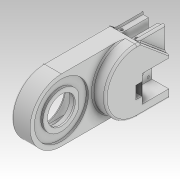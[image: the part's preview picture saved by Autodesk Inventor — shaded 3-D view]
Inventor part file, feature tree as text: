
AUTODESK INVENTOR PART (.ipt)
format: ipt  version: 2020 (Build 240168000, 168)  size: 802,304 bytes
history: native  units: mm
features: sketch x33, extrude x31, chamfer x4, fillet x3, plane x2, revolve x2, projected_geometry x1
ambient origin geometry x8: Origin, YZ Plane, XZ Plane, XY Plane, X Axis, Y Axis, Z Axis, Center Point
bodies: Solid1 (feature_tree)
feature tree (76):
  extrude  "Extrusion1"  Depth=50.0mm
  extrude  "Extrusion3"  Depth=50.0mm TaperAngle=0.0deg
  extrude  "Extrusion6"  TaperAngle=0.0deg  [1 undecoded]
  extrude  "Extrusion7"  Depth=50.0mm
  extrude  "Extrusion8"  Depth=10.0mm TaperAngle=0.0deg
  extrude  "Extrusion9"  TaperAngle=0.0deg  [1 undecoded]
  extrude  "Extrusion10"  TaperAngle=30.0deg  [1 undecoded]
  extrude  "Extrusion11"  Depth=16.15mm
  extrude  "Extrusion12"  Depth=60.0mm
  plane  "Work Plane1"
  extrude  "Extrusion13"  Depth=10.0mm TaperAngle=0.0deg
  revolve  "Revolution1"  [1 undecoded]
  extrude  "Extrusion14"  Depth=86.0mm
  extrude  "Extrusion15"  Depth=3.5mm TaperAngle=0.0deg
  extrude  "Extrusion16"  Depth=75.0mm
  revolve  "Revolution2"  [1 undecoded]
  extrude  "Extrusion17"  Depth=1.5mm
  fillet  "Fillet1"  [1 undecoded]
  plane  "Work Plane2"
  extrude  "Extrusion18"  Depth=31.0mm
  extrude  "Extrusion19"  Depth=3.0mm TaperAngle=0.0deg
  extrude  "Extrusion20"  Depth=15.0mm TaperAngle=0.0deg
  extrude  "Extrusion21"  Depth=130.0mm
  extrude  "Extrusion25"  Depth=6.0mm TaperAngle=360.0deg
  extrude  "Extrusion22"  Depth=15.0mm
  fillet  "Fillet2"  Radius=5.2mm
  fillet  "Fillet3"  Radius=1.0mm
  extrude  "Extrusion23"  TaperAngle=90.0deg  [1 undecoded]
  extrude  "Extrusion24"  Depth=20.0mm
  extrude  "Extrusion26"  Depth=19.198622mm
  extrude  "Extrusion27"  Depth=50.0mm
  extrude  "Extrusion28"  TaperAngle=0.0deg  [1 undecoded]
  extrude  "CHOP"  Depth=14.0mm
  extrude  "Extrusion30"  Depth=12.5mm
  extrude  "Extrusion31"  Depth=130.0mm
  extrude  "Extrusion32"  Depth=10.0mm
  chamfer  "Chamfer1"  Distance=110.0mm
  chamfer  "Chamfer2"  Distance=3.0mm
  chamfer  "Chamfer3"  Distance=5.0mm
  chamfer  "Chamfer4"  Distance=1.0mm
  extrude  "Extrusion33"  Depth=4.0mm TaperAngle=0.0deg
  extrude  "Extrusion34"  Depth=4.0mm
  sketch  "Sketch1"  dims[d0=50.0mm d1=250.0mm]
  sketch  "Sketch3"  dims[d2=47.2mm d3=50.0mm d4=0.0mm]
  sketch  "Sketch6"  dims[d10=5.0mm d11=0.0mm d12=0.0mm]
  sketch  "Sketch7"  dims[d19=50.0mm d20=0.0mm d21=8.726646mm]
  projected_geometry  "Projected Loop1"
  sketch  "Sketch8"  dims[d22=75.0mm d25=10.0mm d26=0.0mm]
  sketch  "Sketch9"  dims[d27=50.0mm d30=0.0mm d31=0.0mm]
  sketch  "Sketch10"  dims[d33=30.0deg d34=30.0deg]
  sketch  "Sketch11"  dims[d35=0.0mm d36=0.0mm d37=16.15mm]
  sketch  "Sketch12"  dims[d38=3.3mm d39=60.0mm]
  sketch  "Sketch13"  dims[d40=80.0mm d42=360.0deg d44=10.0mm d45=0.0mm]
  sketch  "Sketch14"  dims[d50=42.5mm d51=42.5mm d52=0.0mm d53=0.0mm]
  sketch  "Sketch15"  dims[d54=38.0mm d55=86.0mm]
  sketch  "Sketch16"  dims[d56=59.0mm d57=3.5mm d58=0.0mm]
  sketch  "Sketch17"  dims[d59=-2.0mm d60=75.0mm]
  sketch  "Sketch18"  dims[d61=40.0mm d62=18.0mm d63=0.0mm]
  sketch  "Sketch19"  dims[d64=1.5mm d65=7.3mm d66=90.0deg]
  sketch  "Sketch20"  dims[d67=22.0mm d68=31.0mm]
  sketch  "Sketch21"  dims[d69=3.5mm d70=3.0mm d71=0.0mm]
  sketch  "Sketch22"  dims[d72=0.0mm d73=15.0mm d74=0.0mm]
  sketch  "Sketch23"  dims[d75=15.0mm d76=130.0mm]
  sketch  "Sketch24"  dims[d77=6.0mm d78=80.0mm d80=360.0deg]
  sketch  "Sketch25"  dims[d82=15.0mm d83=0.0mm d84=5.2mm d85=5.2mm d86=1.0mm]
  sketch  "Sketch26"  dims[d87=1.5mm d88=90.0deg]
  sketch  "Sketch27"  dims[d89=5.5mm d90=20.0mm]
  sketch  "Sketch28"  dims[d91=30.0deg d92=19.198622mm]
  sketch  "Sketch29"  dims[d93=15.0mm d94=0.0mm d95=50.0mm]
  sketch  "Sketch30"  dims[d96=30.0mm d97=0.0mm]
  sketch  "Sketch31"  dims[d98=8.0mm d99=14.0mm]
  sketch  "Sketch32"  dims[d100=6.4mm d101=12.5mm]
  sketch  "Sketch33"  dims[d102=130.0mm d103=80.0mm d104=0.0mm d105=0.0mm d106=2.45mm]
  sketch  "Sketch34"  dims[d107=10.0mm d108=10.0mm]
  sketch  "Sketch35"  dims[d109=32.0mm d110=110.0mm d111=0.0mm]
  sketch  "Sketch36"  dims[d112=3.0mm d113=3.0mm d114=5.0mm d115=1.0mm d116=4.0mm d117=0.0mm d118=4.0mm d119=4.0mm d120=32.25mm d121=0.0mm d122=3.0mm d124=0.5mm d125=0.0mm d126=3.0mm d127=2.0mm d128=8.0mm d129=8.0mm d130=4.0mm d131=4.0mm d132=4.3mm d133=6.0mm d134=0.0mm d135=4.0mm d136=0.0mm d137=70.0mm d138=0.5mm d139=0.0mm d140=2.5mm d141=10.0mm d142=20.0mm d143=15.0mm d144=0.0mm d145=8.0mm d146=23.75mm d147=0.0mm d148=15.0mm d149=23.75mm d150=0.0mm d151=200.998mm d152=0.0mm d153=0.0mm d154=0.0mm d155=5.0mm d156=2.0mm d157=45.0deg d158=10.0mm d159=3.5mm d160=0.0mm d161=0.8mm d162=2.0mm d163=45.0deg d164=6.108652mm d165=37.0mm d166=0.0mm d167=0.5mm d168=2.0mm d169=45.0deg d170=10.0mm d171=2.0mm d172=45.0deg d173=0.2mm d174=0.0mm d175=3.5mm d176=0.0mm d123=0.872665mm]
note: 8 required parameter values undecoded (feature->parameter linkage not recoverable at this tier; creation-order binding heuristic only, values carry confidence <= 0.55)